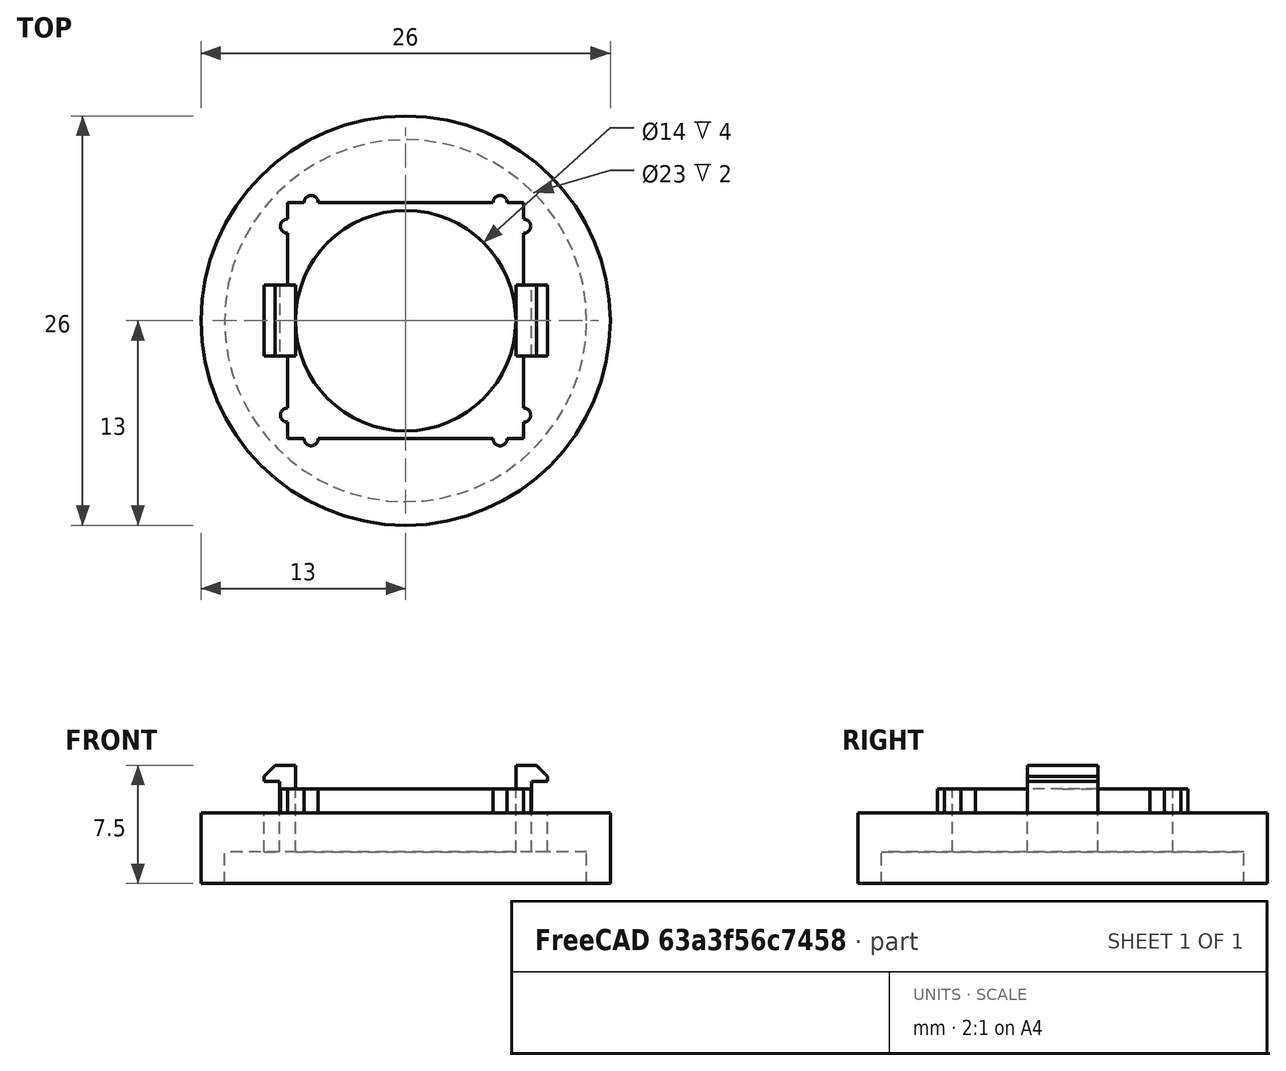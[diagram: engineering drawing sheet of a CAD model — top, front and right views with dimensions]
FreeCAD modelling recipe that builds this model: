
FCSTD DOCUMENT  (FreeCAD 0.19R24276 (Git))
Label: pieza guia careta
License: All rights reserved
LicenseURL: http://en.wikipedia.org/wiki/All_rights_reserved
objects: TechDraw::DrawViewDimension×13, Part::Cylinder×11, TechDraw::DrawProjGroupItem×4, Part::Box×3, Part::MultiFuse×3, Part::Cut×3, Part::FeaturePython×2, TechDraw::DrawSVGTemplate×2, TechDraw::DrawViewPart×2, TechDraw::DrawPage×2, Part::Chamfer×1, TechDraw::DrawProjGroup×1, TechDraw::DrawViewAnnotation×1
note: 23 computed .brp shape members not serialized (recipe doc carries the construction recipe); baked Part::Feature solids carry a one-line shape summary decoded from their .brp

FEATURE [Part::Cylinder] Cylinder  label="Cilindro"
  Angle = 360
  AttacherType = Attacher::AttachEngine3D
  Height = 4.5
  Radius = 13
FEATURE [Part::Box] Box  label="Cubo"
  AttacherType = Attacher::AttachEngine3D
  Height = 2
  Length = 15
  Placement = pos=(-7.5,-7.5,4) rot=(0,0,1;0rad)
  Width = 15
FEATURE [Part::MultiFuse] Fusion
  Shapes = -> [Cylinder,Box]
FEATURE [Part::Cylinder] Cylinder001  label="Cilindro001"
  Angle = 360
  AttacherType = Attacher::AttachEngine3D
  Height = 2
  Radius = 11.5
FEATURE [Part::Cut] Cut
  Base = -> Fusion
  Tool = -> Cylinder001
FEATURE [Part::Cylinder] Cylinder002  label="Cilindro002"
  Angle = 360
  AttacherType = Attacher::AttachEngine3D
  Height = 10
  Radius = 7
FEATURE [Part::Cut] Cut001
  Base = -> Cut
  Tool = -> Cylinder002
FEATURE [Part::Cylinder] Cylinder003  label="Cilindro003"
  Angle = 360
  AttacherType = Attacher::AttachEngine3D
  Height = 2
  Placement = pos=(6,7.5,4) rot=(0,0,1;0rad)
  Radius = 0.45
FEATURE [Part::Cylinder] Cylinder004  label="Cilindro004"
  Angle = 360
  AttacherType = Attacher::AttachEngine3D
  Height = 2
  Placement = pos=(-6,7.5,4) rot=(0,0,1;0rad)
  Radius = 0.45
FEATURE [Part::Cylinder] Cylinder005  label="Cilindro005"
  Angle = 360
  AttacherType = Attacher::AttachEngine3D
  Height = 2
  Placement = pos=(6,-7.5,4) rot=(0,0,1;0rad)
  Radius = 0.45
FEATURE [Part::Cylinder] Cylinder006  label="Cilindro006"
  Angle = 360
  AttacherType = Attacher::AttachEngine3D
  Height = 2
  Placement = pos=(-6,-7.5,4) rot=(0,0,1;0rad)
  Radius = 0.45
FEATURE [Part::Cylinder] Cylinder007  label="Cilindro007"
  Angle = 360
  AttacherType = Attacher::AttachEngine3D
  Height = 2
  Placement = pos=(7.5,6,4) rot=(0,0,1;0rad)
  Radius = 0.45
FEATURE [Part::Cylinder] Cylinder008  label="Cilindro008"
  Angle = 360
  AttacherType = Attacher::AttachEngine3D
  Height = 2
  Placement = pos=(-7.5,6,4) rot=(0,0,1;0rad)
  Radius = 0.45
FEATURE [Part::Cylinder] Cylinder009  label="Cilindro009"
  Angle = 360
  AttacherType = Attacher::AttachEngine3D
  Height = 2
  Placement = pos=(7.5,-6,4) rot=(0,0,1;0rad)
  Radius = 0.45
FEATURE [Part::Cylinder] Cylinder010  label="Cilindro010"
  Angle = 360
  AttacherType = Attacher::AttachEngine3D
  Height = 2
  Placement = pos=(-7.5,-6,4) rot=(0,0,1;0rad)
  Radius = 0.45
FEATURE [Part::MultiFuse] Fusion001
  Shapes = -> [Cut001,Cylinder003,Cylinder004,Cylinder005,Cylinder006,Cylinder007,Cylinder008,Cylinder009,Cylinder010]
FEATURE [Part::Box] Box001  label="Cubo001"
  AttacherType = Attacher::AttachEngine3D
  Height = 5.5
  Length = 2
  Placement = pos=(7,-2.25,2) rot=(0,0,1;0rad)
  Width = 4.5
FEATURE [Part::Box] Box002  label="Cubo002"
  AttacherType = Attacher::AttachEngine3D
  Height = 5.75
  Length = 1
  Placement = pos=(8,-2.25,0.75) rot=(0,0,1;0rad)
  Width = 4.5
FEATURE [Part::FeaturePython] Array  # Draft array (typed FeaturePython)
  Angle = 360
  ArrayType = 1
  Axis = (0,0,1)
  Base = -> Box001
  Center = (0,0,0)
  Fuse = false
  IntervalAxis = (0,0,0)
  IntervalX = (1,0,0)
  IntervalY = (0,1,0)
  IntervalZ = (0,0,0)
  NumberPolar = 2
  NumberX = 2
  NumberY = 2
  NumberZ = 1
FEATURE [Part::FeaturePython] Array001  # Draft array (typed FeaturePython)
  Angle = 360
  ArrayType = 1
  Axis = (0,0,1)
  Base = -> Box002
  Center = (0,0,0)
  Fuse = false
  IntervalAxis = (0,0,0)
  IntervalX = (1,0,0)
  IntervalY = (0,1,0)
  IntervalZ = (0,0,0)
  NumberPolar = 2
  NumberX = 2
  NumberY = 2
  NumberZ = 1
FEATURE [Part::MultiFuse] Fusion002
  Shapes = -> [Fusion001,Array]
FEATURE [Part::Cut] Cut002
  Base = -> Fusion002
  Tool = -> Array001
FEATURE [Part::Chamfer] Chamfer
  Base = -> Cut002
  Edges = 2 edges r=0.7: [Edge130,Edge141]
FEATURE [TechDraw::DrawSVGTemplate] Template
  EditableTexts = Designed_by_Name=<owner>; Drawing_number=001; FC-Date=-; FC-SC=1:1; FC-SH=9/10; FC-Title=GuidePiece; Subtitle=Pieza Guia; Weight=<100gr
  Height = 210
  Orientation = 1
  Width = 297
FEATURE [TechDraw::DrawSVGTemplate] Template001
  EditableTexts = Designed_by_Name=<owner>; Drawing_number=001; FC-Date=-; FC-SC=4:1; FC-SH=10/10; FC-Title=GuidePiece; Subtitle=Pieza Guia; Weight=<100gr
  Height = 210
  Orientation = 1
  Width = 297
FEATURE [TechDraw::DrawViewPart] View
  CoarseView = false
  Direction = (0.577,-0.577,0.577)
  Focus = 100
  HardHidden = false
  IsoCount = 0
  IsoHidden = false
  IsoVisible = false
  LockPosition = false
  Perspective = false
  Rotation = 0
  Scale = 4
  ScaleType = 0
  SeamHidden = false
  SeamVisible = true
  SmoothHidden = false
  SmoothVisible = true
  Source = -> [Chamfer]
  X = 208.11
  XDirection = (0.707,0.707,0)
  Y = 136.169
FEATURE [TechDraw::DrawViewPart] View001
  CoarseView = false
  Direction = (0.577,-0.577,0.577)
  Focus = 100
  HardHidden = false
  IsoCount = 0
  IsoHidden = false
  IsoVisible = false
  LockPosition = false
  Perspective = false
  Rotation = 0
  Scale = 4
  ScaleType = 0
  SeamHidden = false
  SeamVisible = true
  SmoothHidden = false
  SmoothVisible = true
  Source = -> [Chamfer]
  X = 143.412
  XDirection = (0.707,0.707,0)
  Y = 137.288
FEATURE [TechDraw::DrawProjGroupItem] ProjItem  label="Front"
  CoarseView = false
  Direction = (0,-1,0)
  Focus = 100
  HardHidden = false
  IsoCount = 0
  IsoHidden = false
  IsoVisible = false
  LockPosition = true
  Perspective = false
  Rotation = 0
  RotationVector = (1,0,0)
  ScaleType = 2
  SeamHidden = false
  SeamVisible = true
  SmoothHidden = false
  SmoothVisible = true
  Source = -> [Chamfer]
  Type = 0
  X = 0
  XDirection = (1,0,0)
  Y = 0
FEATURE [TechDraw::DrawProjGroupItem] ProjItem001  label="Top"
  CoarseView = false
  Direction = (0,0,1)
  Focus = 100
  HardHidden = false
  IsoCount = 0
  IsoHidden = false
  IsoVisible = false
  LockPosition = false
  Perspective = false
  Rotation = 0
  RotationVector = (1,0,0)
  ScaleType = 2
  SeamHidden = false
  SeamVisible = true
  SmoothHidden = false
  SmoothVisible = true
  Source = -> [Chamfer]
  Type = 4
  X = 0
  XDirection = (1,0,0)
  Y = -41
FEATURE [TechDraw::DrawProjGroupItem] ProjItem002  label="Bottom"
  CoarseView = false
  Direction = (0,0,-1)
  Focus = 100
  HardHidden = false
  IsoCount = 0
  IsoHidden = false
  IsoVisible = false
  LockPosition = false
  Perspective = false
  Rotation = 0
  RotationVector = (1,0,0)
  ScaleType = 2
  SeamHidden = false
  SeamVisible = true
  SmoothHidden = false
  SmoothVisible = true
  Source = -> [Chamfer]
  Type = 5
  X = 0
  XDirection = (1,0,0)
  Y = 41
FEATURE [TechDraw::DrawProjGroupItem] ProjItem003  label="Right"
  CoarseView = false
  Direction = (1,-1e-16,0)
  Focus = 100
  HardHidden = false
  IsoCount = 0
  IsoHidden = false
  IsoVisible = false
  LockPosition = false
  Perspective = false
  Rotation = 0
  RotationVector = (1,0,0)
  ScaleType = 2
  SeamHidden = false
  SeamVisible = true
  SmoothHidden = false
  SmoothVisible = true
  Source = -> [Chamfer]
  Type = 2
  X = -41
  XDirection = (1e-16,1,0)
  Y = 0
FEATURE [TechDraw::DrawProjGroup] ProjGroup
  Anchor = -> ProjItem
  AutoDistribute = true
  LockPosition = false
  ProjectionType = 0
  Rotation = 0
  ScaleType = 0
  Source = -> [Chamfer]
  Views = -> [ProjItem,ProjItem001,ProjItem002,ProjItem003]
  X = 102.916
  Y = 115.909
  spacingX = 15
  spacingY = 15
FEATURE [TechDraw::DrawViewDimension] Dimension
  Arbitrary = false
  ArbitraryTolerances = false
  EqualTolerance = true
  FormatSpec = %.2f
  FormatSpecOverTolerance = %+.2f
  FormatSpecUnderTolerance = %+.2f
  Inverted = false
  LockPosition = false
  MeasureType = 1
  OverTolerance = 0
  References2D = -> [ProjItem]
  Rotation = 0
  ScaleType = 0
  TheoreticalExact = false
  Type = 1
  UnderTolerance = 0
  X = -3.64124
  Y = -12.8075
FEATURE [TechDraw::DrawViewDimension] Dimension001
  Arbitrary = false
  ArbitraryTolerances = false
  EqualTolerance = true
  FormatSpec = %.2f
  FormatSpecOverTolerance = %+.2f
  FormatSpecUnderTolerance = %+.2f
  Inverted = false
  LockPosition = false
  MeasureType = 1
  OverTolerance = 0
  References2D = -> [ProjItem]
  Rotation = 0
  ScaleType = 0
  TheoreticalExact = false
  Type = 2
  UnderTolerance = 0
  X = 20.436
  Y = -3.08077
FEATURE [TechDraw::DrawViewDimension] Dimension002
  Arbitrary = false
  ArbitraryTolerances = false
  EqualTolerance = true
  FormatSpec = ⌀%.2f
  FormatSpecOverTolerance = %+.2f
  FormatSpecUnderTolerance = %+.2f
  Inverted = false
  LockPosition = false
  MeasureType = 1
  OverTolerance = 0
  References2D = -> [ProjItem001]
  Rotation = 0
  ScaleType = 0
  TheoreticalExact = false
  Type = 5
  UnderTolerance = 0
  X = 26.9218
  Y = 12.5964
FEATURE [TechDraw::DrawViewDimension] Dimension003
  Arbitrary = false
  ArbitraryTolerances = false
  EqualTolerance = true
  FormatSpec = ⌀%.2f
  FormatSpecOverTolerance = %+.2f
  FormatSpecUnderTolerance = %+.2f
  Inverted = false
  LockPosition = false
  MeasureType = 1
  OverTolerance = 0
  References2D = -> [ProjItem002]
  Rotation = 0
  ScaleType = 0
  TheoreticalExact = false
  Type = 5
  UnderTolerance = 0
  X = 30.2533
  Y = 17.3285
FEATURE [TechDraw::DrawPage] Page  label="Vistas"
  KeepUpdated = true
  NextBalloonIndex = 1
  ProjectionType = 0
  Template = -> Template
  Views = -> [View,ProjGroup,Dimension,Dimension001,Dimension002,Dimension003]
FEATURE [TechDraw::DrawViewAnnotation] Annotation
  Font = osifont
  LineSpace = 80
  LockPosition = false
  MaxWidth = -1
  Rotation = 0
  ScaleType = 0
  Text = Aproximate measurements: | Check with 3D piece
  TextSize = 5
  TextStyle = 0
  X = 84.9
  Y = 69.4
FEATURE [TechDraw::DrawViewDimension] Dimension004
  Arbitrary = false
  ArbitraryTolerances = false
  EqualTolerance = true
  FormatSpec = %.2f
  FormatSpecOverTolerance = %+.2f
  FormatSpecUnderTolerance = %+.2f
  Inverted = false
  LockPosition = false
  MeasureType = 1
  OverTolerance = 0
  References2D = -> [View001]
  Rotation = 0
  ScaleType = 0
  TheoreticalExact = false
  Type = 2
  UnderTolerance = 0
  X = 70.5658
  Y = -41.3678
FEATURE [TechDraw::DrawViewDimension] Dimension005
  Arbitrary = false
  ArbitraryTolerances = false
  EqualTolerance = true
  FormatSpec = %.2f
  FormatSpecOverTolerance = %+.2f
  FormatSpecUnderTolerance = %+.2f
  Inverted = false
  LockPosition = false
  MeasureType = 1
  OverTolerance = 0
  References2D = -> [View001]
  Rotation = 0
  ScaleType = 0
  TheoreticalExact = false
  Type = 2
  UnderTolerance = 0
  X = -81.5468
  Y = -3.85945
FEATURE [TechDraw::DrawViewDimension] Dimension006
  Arbitrary = false
  ArbitraryTolerances = false
  EqualTolerance = true
  FormatSpec = %.2f
  FormatSpecOverTolerance = %+.2f
  FormatSpecUnderTolerance = %+.2f
  Inverted = false
  LockPosition = false
  MeasureType = 1
  OverTolerance = 0
  References2D = -> [View001]
  Rotation = 0
  ScaleType = 0
  TheoreticalExact = false
  Type = 0
  UnderTolerance = 0
  X = -26.3058
  Y = -6.94444
FEATURE [TechDraw::DrawViewDimension] Dimension007
  Arbitrary = false
  ArbitraryTolerances = false
  EqualTolerance = true
  FormatSpec = ⌀%.2f
  FormatSpecOverTolerance = %+.2f
  FormatSpecUnderTolerance = %+.2f
  Inverted = false
  LockPosition = false
  MeasureType = 1
  OverTolerance = 0
  References2D = -> [View001]
  Rotation = 0
  ScaleType = 0
  TheoreticalExact = false
  Type = 5
  UnderTolerance = 0
  X = -24.1997
  Y = -24.9149
FEATURE [TechDraw::DrawViewDimension] Dimension008
  Arbitrary = false
  ArbitraryTolerances = false
  EqualTolerance = true
  FormatSpec = %.2f
  FormatSpecOverTolerance = %+.2f
  FormatSpecUnderTolerance = %+.2f
  Inverted = false
  LockPosition = false
  MeasureType = 1
  OverTolerance = 0
  References2D = -> [View001]
  Rotation = 0
  ScaleType = 0
  TheoreticalExact = false
  Type = 2
  UnderTolerance = 0
  X = 0.708906
  Y = 12.5555
FEATURE [TechDraw::DrawViewDimension] Dimension009
  Arbitrary = false
  ArbitraryTolerances = false
  EqualTolerance = true
  FormatSpec = %.2f
  FormatSpecOverTolerance = %+.2f
  FormatSpecUnderTolerance = %+.2f
  Inverted = false
  LockPosition = false
  MeasureType = 1
  OverTolerance = 0
  References2D = -> [View001]
  Rotation = 0
  ScaleType = 0
  TheoreticalExact = false
  Type = 6
  UnderTolerance = 0
  X = 24.9729
  Y = 0.893062
FEATURE [TechDraw::DrawViewDimension] Dimension010
  Arbitrary = false
  ArbitraryTolerances = false
  EqualTolerance = true
  FormatSpec = %.2f
  FormatSpecOverTolerance = %+.2f
  FormatSpecUnderTolerance = %+.2f
  Inverted = false
  LockPosition = false
  MeasureType = 1
  OverTolerance = 0
  References2D = -> [View001]
  Rotation = 0
  ScaleType = 0
  TheoreticalExact = false
  Type = 0
  UnderTolerance = 0
  X = 20.7661
  Y = -14.9331
FEATURE [TechDraw::DrawViewDimension] Dimension011
  Arbitrary = false
  ArbitraryTolerances = false
  EqualTolerance = true
  FormatSpec = %.2f
  FormatSpecOverTolerance = %+.2f
  FormatSpecUnderTolerance = %+.2f
  Inverted = false
  LockPosition = false
  MeasureType = 1
  OverTolerance = 0
  References2D = -> [View001]
  Rotation = 0
  ScaleType = 0
  TheoreticalExact = false
  Type = 0
  UnderTolerance = 0
  X = -0.970994
  Y = -24.6616
FEATURE [TechDraw::DrawViewDimension] Dimension012
  Arbitrary = false
  ArbitraryTolerances = false
  EqualTolerance = true
  FormatSpec = %.2f
  FormatSpecOverTolerance = %+.2f
  FormatSpecUnderTolerance = %+.2f
  Inverted = false
  LockPosition = false
  MeasureType = 1
  OverTolerance = 0
  References2D = -> [View001]
  Rotation = 0
  ScaleType = 0
  TheoreticalExact = false
  Type = 0
  UnderTolerance = 0
  X = 57.1376
  Y = 26.7477
FEATURE [TechDraw::DrawPage] Page001  label="Cotas"
  KeepUpdated = true
  NextBalloonIndex = 1
  ProjectionType = 0
  Template = -> Template001
  Views = -> [View001,Annotation,Dimension004,Dimension005,Dimension006,Dimension007,Dimension008,Dimension009,Dimension010,Dimension011,Dimension012]
